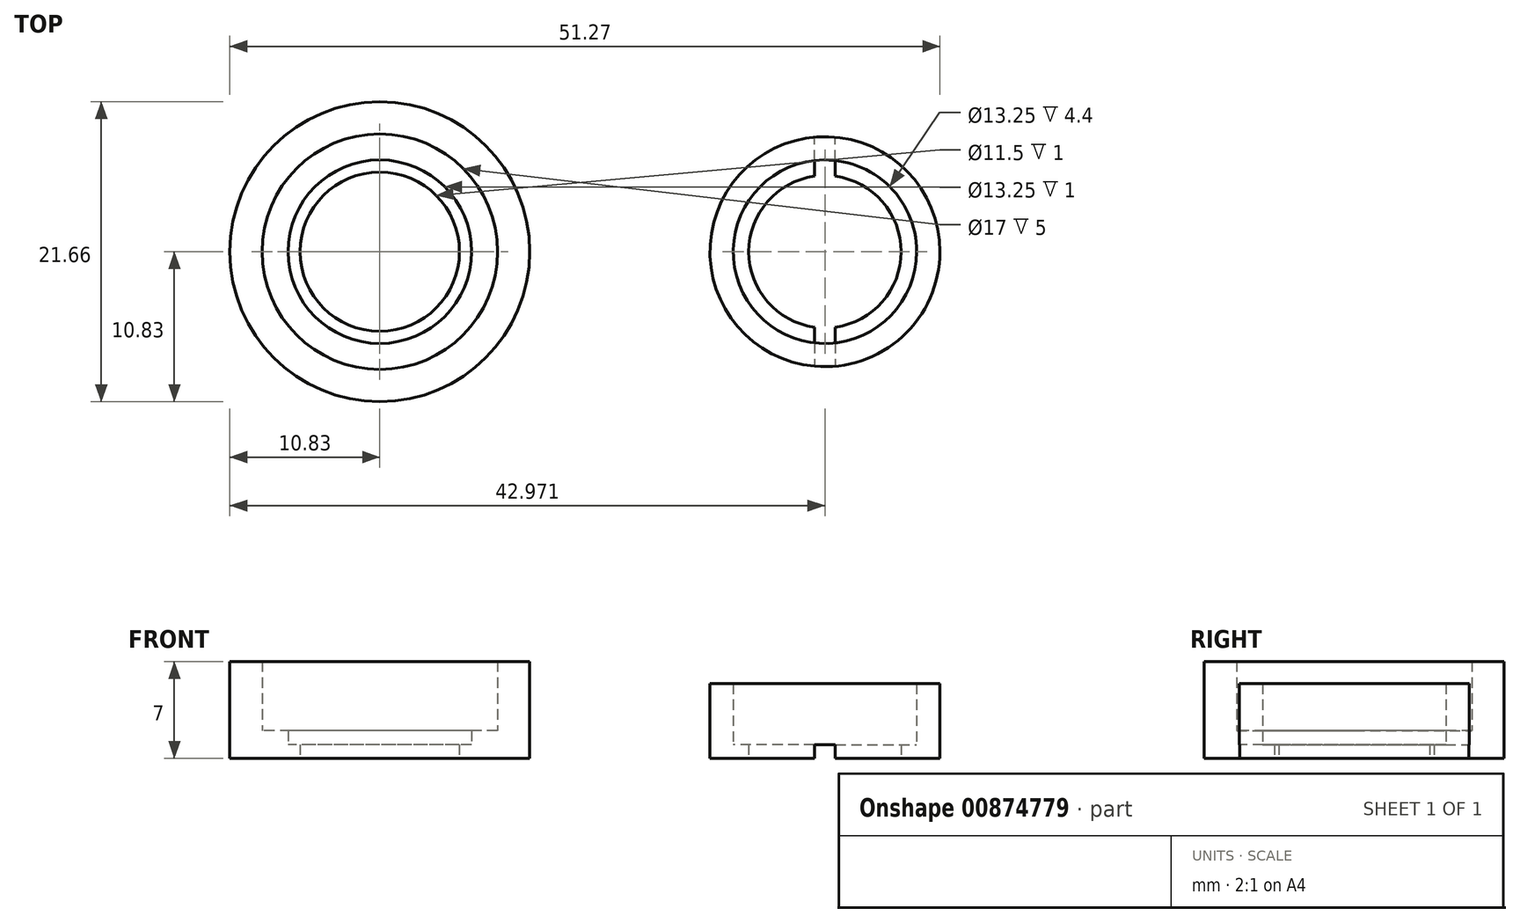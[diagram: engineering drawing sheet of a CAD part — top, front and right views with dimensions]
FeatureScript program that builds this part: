
annotation { "Feature Type Name" : "Feature", "Feature Type Description" : "" }
export const myFeature = defineFeature(function(context is Context, id is Id, definition is map)
    precondition{}
    {
        {
            var Q0;
            Q0=qCreatedBy(makeId("Top.planeOp"),FACE);
            var sketch = newSketch(context, id + "F0", { "sketchPlane" : qUnion([Q0])});
            skCircle(sketch, "E0", {"center": v(0, 0) * mm, "radius": 10.82 * mm});
            skCircle(sketch, "E1", {"center": v(0, 0) * mm, "radius": 5.75 * mm});
            skSolve(sketch);
        }
        {
            var Q0;
            Q0 = qSketchRegion(id + "F0", true);
            extrude(context, id + "F1", {"entities" : qUnion([Q0]), "depth" : 1 * mm, "offsetDistance" : 25 * mm});
        }
        {
            var Q0;
            Q0=makeQuery(id+"F1.opExtrude","CAP_FACE",FACE,{"disambiguationData":[OSD([sQuery(id+"F0.wireOp",EDGE,"E0"),sQuery(id+"F0.wireOp",EDGE,"E1")])],"isStart":false});
            var sketch = newSketch(context, id + "F2", { "sketchPlane" : qUnion([Q0])});
            skCircle(sketch, "E2", {"center": v(0, 0) * mm, "radius": 6.62 * mm});
            skSolve(sketch);
        }
        {
            var Q0;
            Q0=makeQuery(id+"F2.imprint","IMPRINT",FACE,{"disambiguationData":[TD([[makeQuery(id+"F2.imprint","IMPRINT",EDGE,{"derivedFrom":sQuery(id+"F2.wireOp",EDGE,"E2")}),-1.0]])]});
            extrude(context, id + "F3", {"entities" : qUnion([Q0]), "operationType" : NewBodyOperationType.ADD, "depth" : 1 * mm, "offsetDistance" : 25 * mm});
        }
        {
            var Q0;
            Q0=makeQuery(id+"F3.opExtrude","CAP_FACE",FACE,{"disambiguationData":[OSD([sQuery(id+"F0.wireOp",EDGE,"E0"),sQuery(id+"F2.wireOp",EDGE,"E2")])],"isStart":false});
            var sketch = newSketch(context, id + "F4", { "sketchPlane" : qUnion([Q0])});
            skCircle(sketch, "E3", {"center": v(0, 0) * mm, "radius": 8.5 * mm});
            skSolve(sketch);
        }
        {
            var Q0;
            Q0=makeQuery(id+"F4.imprint","IMPRINT",FACE,{"disambiguationData":[TD([[makeQuery(id+"F4.imprint","IMPRINT",EDGE,{"derivedFrom":sQuery(id+"F4.wireOp",EDGE,"E3")}),-1.0]])]});
            extrude(context, id + "F5", {"entities" : qUnion([Q0]), "operationType" : NewBodyOperationType.ADD, "depth" : 5 * mm, "offsetDistance" : 25 * mm});
        }
        {
            var Q0;
            Q0=qCreatedBy(makeId("Top.planeOp"),FACE);
            var sketch = newSketch(context, id + "F6", { "sketchPlane" : qUnion([Q0])});
            skCircle(sketch, "E4", {"center": v(32.14, 0) * mm, "radius": 8.3 * mm});
            skCircle(sketch, "E5", {"center": v(32.14, 0) * mm, "radius": 5.5 * mm});
            skSolve(sketch);
        }
        {
            var Q0;
            Q0=makeQuery(id+"F6.imprint","IMPRINT",FACE,{"disambiguationData":[TD([[makeQuery(id+"F6.imprint","IMPRINT",EDGE,{"derivedFrom":sQuery(id+"F6.wireOp",EDGE,"E4")}),1.0]])]});
            extrude(context, id + "F7", {"entities" : qUnion([Q0]), "depth" : 1 * mm, "offsetDistance" : 25 * mm});
        }
        {
            var Q0;
            Q0=makeQuery(id+"F7.opExtrude","CAP_FACE",FACE,{"disambiguationData":[OSD([sQuery(id+"F6.wireOp",EDGE,"E4"),sQuery(id+"F6.wireOp",EDGE,"E5")])],"isStart":false});
            var sketch = newSketch(context, id + "F8", { "sketchPlane" : qUnion([Q0])});
            skCircle(sketch, "E6", {"center": v(32.14, 0) * mm, "radius": 6.62 * mm});
            skSolve(sketch);
        }
        {
            var Q0;
            Q0=makeQuery(id+"F8.imprint","IMPRINT",FACE,{"disambiguationData":[TD([[makeQuery(id+"F8.imprint","IMPRINT",EDGE,{"derivedFrom":sQuery(id+"F8.wireOp",EDGE,"E6")}),-1.0]])]});
            extrude(context, id + "F9", {"entities" : qUnion([Q0]), "operationType" : NewBodyOperationType.ADD, "depth" : 4.4 * mm, "offsetDistance" : 25 * mm});
        }
        {
            var Q0;
            Q0=makeQuery(id+"F7.opExtrude","CAP_FACE",FACE,{"disambiguationData":[OSD([sQuery(id+"F6.wireOp",EDGE,"E4"),sQuery(id+"F6.wireOp",EDGE,"E5")])],"isStart":true});
            var sketch = newSketch(context, id + "F10", { "sketchPlane" : qUnion([Q0])});
            skLineSegment(sketch, "E7", {"start": v(32.14, 0) * mm, "end": v(32.9, 0) * mm});
            skLineSegment(sketch, "E8", {"start": v(32.14, 0) * mm, "end": v(31.4, 0) * mm});
            skLineSegment(sketch, "E9", {"start": v(31.4, 0) * mm, "end": v(31.4, 8.27) * mm});
            skLineSegment(sketch, "E10", {"start": v(31.4, 0) * mm, "end": v(31.4, -8.27) * mm});
            skLineSegment(sketch, "E11", {"start": v(32.9, 0) * mm, "end": v(32.9, 8.27) * mm});
            skLineSegment(sketch, "E12", {"start": v(32.9, 0) * mm, "end": v(32.9, -8.27) * mm});
            skSolve(sketch);
        }
        {
            var Q0;
            {var subQ0=sQuery(id+"F10.wireOp",EDGE,"E9");var subQ1=makeQuery(id+"F7.opExtrude","CAP_EDGE",EDGE,{"disambiguationData":[OSD([sQuery(id+"F6.wireOp",EDGE,"E4")])],"isStart":true});var subQ2=makeQuery(id+"F10.imprint","INTERSECT",VERTEX,{"derivedFrom":[subQ1,subQ0]});Q0=makeQuery(id+"F10.imprint","IMPRINT",FACE,{"disambiguationData":[TD([[makeQuery(id+"F10.imprint","IMPRINT",EDGE,{"disambiguationData":[TD([[subQ2,1.0]])],"derivedFrom":subQ0}),-1.0]])]});}
            var Q1;
            {var subQ0=sQuery(id+"F10.wireOp",EDGE,"E10");var subQ1=makeQuery(id+"F7.opExtrude","CAP_EDGE",EDGE,{"disambiguationData":[OSD([sQuery(id+"F6.wireOp",EDGE,"E4")])],"isStart":true});var subQ2=makeQuery(id+"F10.imprint","INTERSECT",VERTEX,{"derivedFrom":[subQ1,subQ0]});Q1=makeQuery(id+"F10.imprint","IMPRINT",FACE,{"disambiguationData":[TD([[makeQuery(id+"F10.imprint","IMPRINT",EDGE,{"disambiguationData":[TD([[subQ2,1.0]])],"derivedFrom":subQ0}),1.0]])]});}
            extrude(context, id + "F11", {"entities" : qUnion([Q0, Q1]), "operationType" : NewBodyOperationType.REMOVE, "oppositeDirection" : true, "depth" : 1 * mm, "offsetDistance" : 25 * mm});
        }
    });
